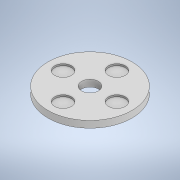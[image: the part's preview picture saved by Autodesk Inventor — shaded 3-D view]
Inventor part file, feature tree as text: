
AUTODESK INVENTOR PART (.ipt)
format: ipt  version: 2020 (Build 240168000, 168)  size: 130,048 bytes
history: native  units: mm
features: extrude x7, sketch x7
ambient origin geometry x8: Origin, YZ Plane, XZ Plane, XY Plane, X Axis, Y Axis, Z Axis, Center Point
bodies: Solid1 (feature_tree)
feature tree (14):
  extrude  "Extrusion1"  Depth=20.0mm
  extrude  "Extrusion2"  Depth=20.0mm
  extrude  "Extrusion3"  Depth=20.0mm
  extrude  "Extrusion4"  Depth=5.0mm TaperAngle=0.0deg
  extrude  "Extrusion5"  Depth=50.0mm
  extrude  "Extrusion6"  Depth=5.0mm
  extrude  "Extrusion7"  Depth=5.0mm TaperAngle=0.0deg
  sketch  "Sketch1"  dims[d1=20.0mm d2=0.0mm d3=250.0mm]
  sketch  "Sketch2"  dims[d4=20.0mm d5=0.0mm d6=50.0mm]
  sketch  "Sketch3"  dims[d7=20.0mm d8=0.0mm d9=80.0mm]
  sketch  "Sketch4"  dims[d10=50.0mm d11=5.0mm d12=0.0mm]
  sketch  "Sketch5"  dims[d13=80.0mm d14=50.0mm]
  sketch  "Sketch6"  dims[d15=5.0mm d16=0.0mm d17=80.0mm]
  sketch  "Sketch7"  dims[d18=50.0mm d19=5.0mm d20=0.0mm d21=80.0mm d22=50.0mm d23=5.0mm d24=0.0mm]
